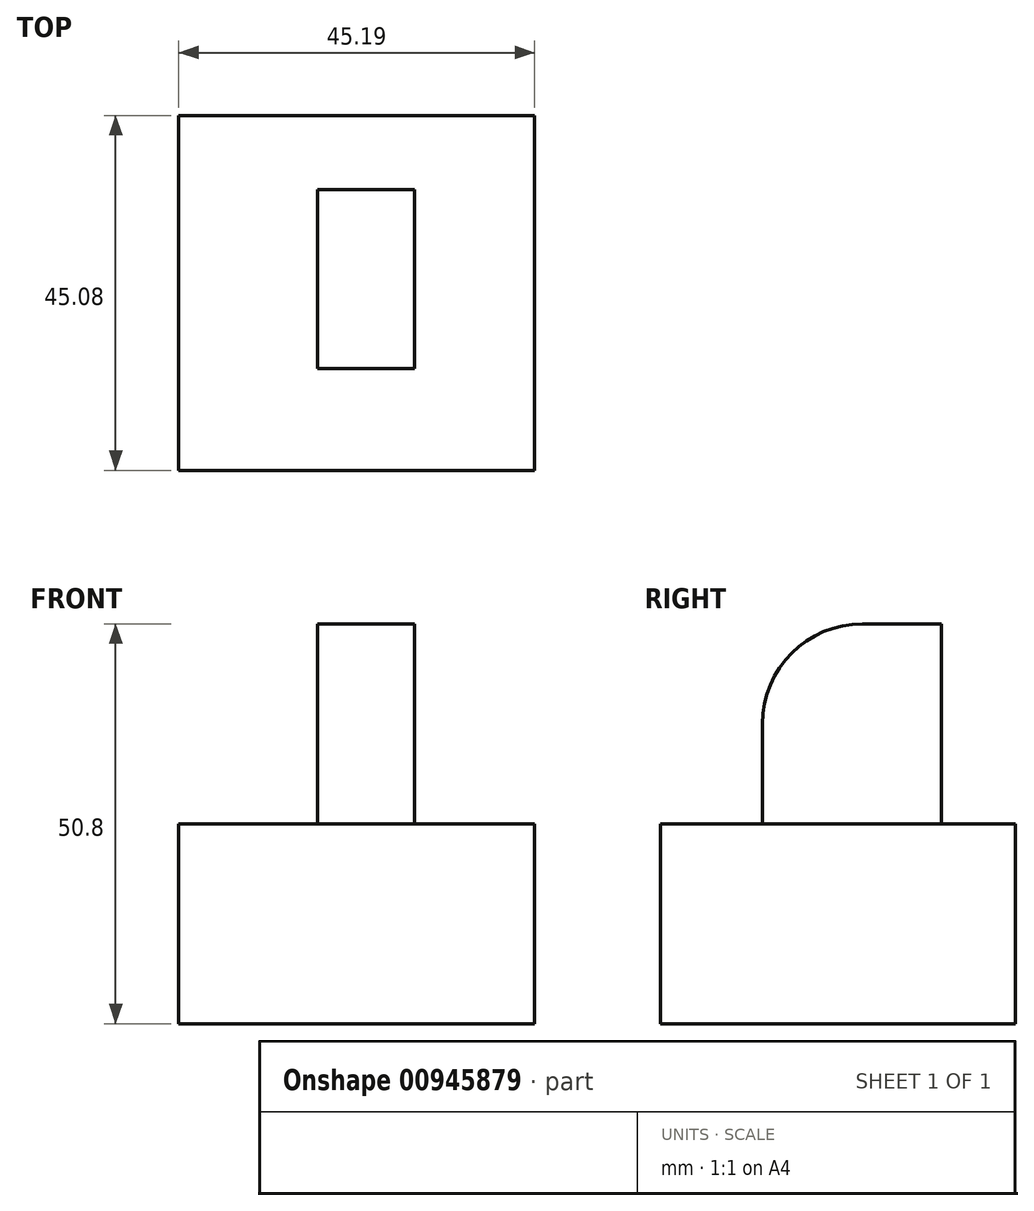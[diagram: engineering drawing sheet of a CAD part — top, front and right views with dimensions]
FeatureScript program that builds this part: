
annotation { "Feature Type Name" : "Feature", "Feature Type Description" : "" }
export const myFeature = defineFeature(function(context is Context, id is Id, definition is map)
    precondition{}
    {
        {
            var Q0;
            Q0=qCreatedBy(makeId("Top.planeOp"),FACE);
            var sketch = newSketch(context, id + "F0", { "sketchPlane" : qUnion([Q0])});
            skLineSegment(sketch, "E0.bottom", {"start": v(-22.6, -26.95) * mm, "end": v(22.6, -26.95) * mm});
            skLineSegment(sketch, "E0.top", {"start": v(-22.6, 18.13) * mm, "end": v(22.6, 18.13) * mm});
            skLineSegment(sketch, "E0.left", {"start": v(-22.6, -26.95) * mm, "end": v(-22.6, 18.13) * mm});
            skLineSegment(sketch, "E0.right", {"start": v(22.6, -26.95) * mm, "end": v(22.6, 18.13) * mm});
            skSolve(sketch);
        }
        {
            var Q0;
            Q0 = qSketchRegion(id + "F0", true);
            extrude(context, id + "F1", {"entities" : qUnion([Q0]), "depth" : 25.4 * mm, "offsetDistance" : 25.4 * mm});
        }
        {
            var Q0;
            Q0=makeQuery(id+"F1.opExtrude","CAP_FACE",FACE,{"disambiguationData":[OSD([sQuery(id+"F0.wireOp",EDGE,"E0.bottom"),sQuery(id+"F0.wireOp",EDGE,"E0.top"),sQuery(id+"F0.wireOp",EDGE,"E0.left"),sQuery(id+"F0.wireOp",EDGE,"E0.right")])],"isStart":false});
            var sketch = newSketch(context, id + "F2", { "sketchPlane" : qUnion([Q0])});
            skLineSegment(sketch, "E1.bottom", {"start": v(-4.98, -14) * mm, "end": v(7.34, -14) * mm});
            skLineSegment(sketch, "E1.top", {"start": v(-4.98, 8.72) * mm, "end": v(7.34, 8.72) * mm});
            skLineSegment(sketch, "E1.left", {"start": v(-4.98, -14) * mm, "end": v(-4.98, 8.72) * mm});
            skLineSegment(sketch, "E1.right", {"start": v(7.34, -14) * mm, "end": v(7.34, 8.72) * mm});
            skSolve(sketch);
        }
        {
            var Q0;
            Q0 = qSketchRegion(id + "F2", true);
            extrude(context, id + "F3", {"entities" : qUnion([Q0]), "operationType" : NewBodyOperationType.ADD, "depth" : 25.4 * mm, "offsetDistance" : 25.4 * mm});
        }
        {
            var Q0;
            Q0=makeQuery(id+"F3.opExtrude","CAP_EDGE",EDGE,{"disambiguationData":[OSD([sQuery(id+"F2.wireOp",EDGE,"E1.bottom")])],"isStart":false});
            fillet(context, id + "F4", {"entities" : qUnion([Q0]), "radius" : 12.7 * mm, "tangentPropagation" : true, "allowEdgeOverflow" : false});
        }
        {
            var Q0;
            Q0=makeQuery(id+"F3.opExtrude","SWEPT_FACE",FACE,{"disambiguationData":[OSD([sQuery(id+"F2.wireOp",EDGE,"E1.left")])]});
            var sketch = newSketch(context, id + "F5", { "sketchPlane" : qUnion([Q0])});
            skCircle(sketch, "E2", {"center": v(0, 43.13) * mm, "radius": 4.76 * mm});
            skSolve(sketch);
        }
        {
            var Q0;
            Q0=sQuery(id+"F5.wireOp",EDGE,"E2");
            extrude(context, id + "F6", {"bodyType" : ToolBodyType.SURFACE, "surfaceEntities" : qUnion([Q0]), "oppositeDirection" : true, "depth" : 11.43 * mm, "offsetDistance" : 25.4 * mm});
        }
    });
